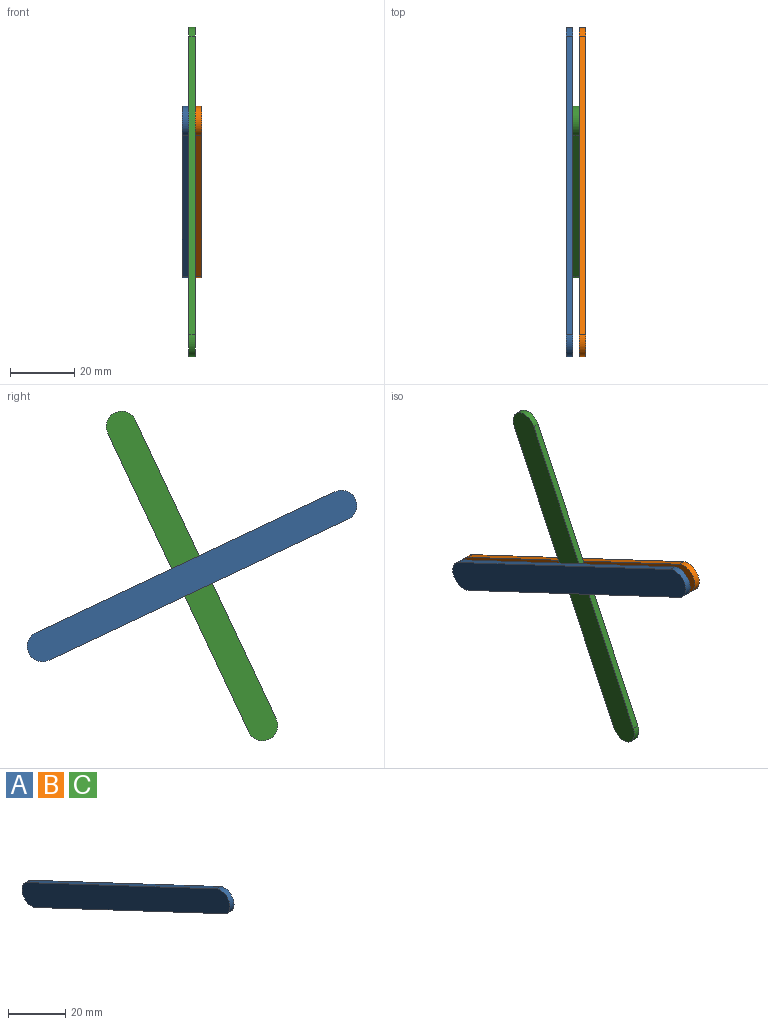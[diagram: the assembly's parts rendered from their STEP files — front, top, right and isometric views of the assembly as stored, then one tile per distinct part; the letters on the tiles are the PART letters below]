
ASSEMBLY  parts=3 mates=2
PART A: 6 faces, bbox 2x102.9x53.5 mm
  f0: plane 93.34x43.99mm, normal (0,0.43,0.9), area 206.4mm2, adj f1,f3,f4,f5
  f1: cylinder r=4.76mm len=9.07mm, axis (-1,0,0), area 29.9mm2, adj f0,f2,f4,f5
  f2: plane 93.34x43.99mm, normal (0,-0.43,-0.9), area 206.4mm2, adj f1,f3,f4,f5
  f3: cylinder r=4.76mm len=9.07mm, axis (-1,0,0), area 29.9mm2, adj f0,f2,f4,f5
  f4: plane 102.87x53.51mm, normal (1,0,0), area 1054.1mm2, adj f0,f1,f2,f3
  f5: plane 102.87x53.51mm, normal (-1,0,0), area 1054.1mm2, adj f0,f1,f2,f3
PART B: same geometry as A
PART C: same geometry as A
PLACE A t=(-41.5,77.59,148.87)mm
PLACE B t=(-37.5,77.59,148.87)mm
PLACE C rot(axis=(1,0,0),90deg) t=(-39.5,147.45,-322.56)mm
MATE fastened C.f4 <-> B.f5  axis (1,0,0) through (-37.5,348.23,-51.92)mm
MATE fastened C.f5 <-> A.f4  axis (-1,0,0) through (-39.5,348.23,-51.92)mm
